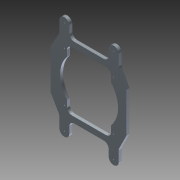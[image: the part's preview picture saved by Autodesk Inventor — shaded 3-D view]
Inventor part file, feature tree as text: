
AUTODESK INVENTOR PART (.ipt)
format: ipt  version: 2015 (Build 190159000, 159)  size: 310,784 bytes
history: native  units: in
note: dims shown in document units (in); Inventor stores cm internally (conversion verified against a paired STEP export)
features: direct_edit x5, move_body x5, other x4, extrude x1, imported_body x1, sketch x1
ambient origin geometry x8: Origin, YZ Plane, XZ Plane, XY Plane, X Axis, Y Axis, Z Axis, Center Point
bodies: Body1 (feature_tree)
feature tree (17):
  other  "BetaSkeletonV011"
  direct_edit  "Direct Edit1"
  direct_edit  "Direct Edit2"
  direct_edit  "Direct Edit4"
  direct_edit  "Direct Edit5"
  extrude  "Extrusion1"  Depth=0.0394in
  direct_edit  "Direct Edit6"
  imported_body  "Base1"
  sketch  "Sketch1"  dims[d0=0.0394in d1=0.0394in d2=0.0in d3=0.0in d4=-0.1575in d8=0.0in d9=0.0in d10=0.0059in d11=0.0in d12=0.0in d13=0.0059in d14=2.2835in d15=1.4375in d16=0.0in d17=0.0in d18=0.0in d19=-0.125in d20=0.0in d21=0.0in d22=-0.125in]
  other  "Size1"
  other  "Size2"
  move_body  "Move1"
  move_body  "Move3"
  move_body  "Move4"
  other  "Size3"
  move_body  "Move5"
  move_body  "Move6"
